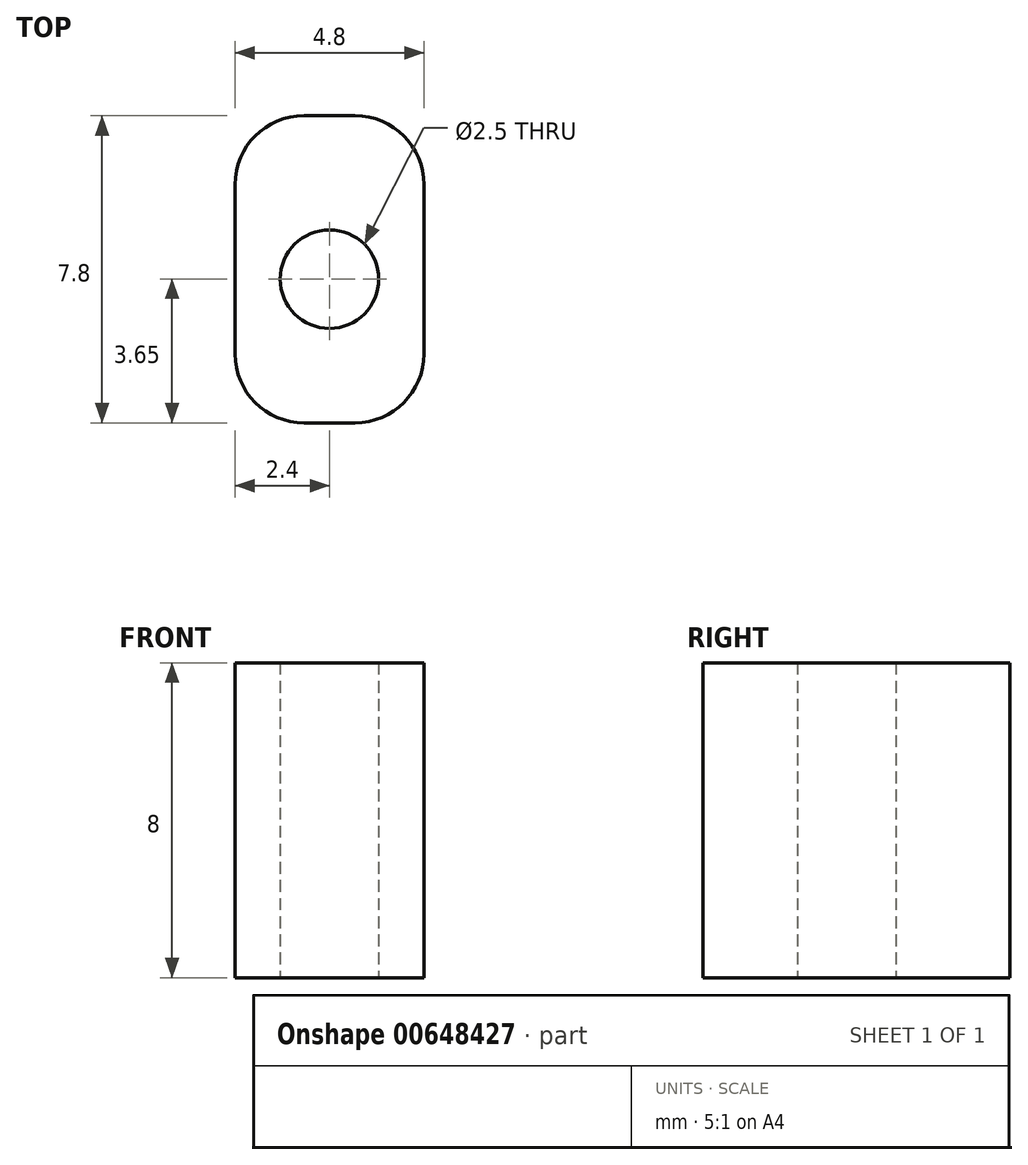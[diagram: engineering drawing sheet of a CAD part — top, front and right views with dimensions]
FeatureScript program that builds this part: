
annotation { "Feature Type Name" : "Feature", "Feature Type Description" : "" }
export const myFeature = defineFeature(function(context is Context, id is Id, definition is map)
    precondition{}
    {
        {
            var Q0;
            Q0=qCreatedBy(makeId("Top.planeOp"),FACE);
            var sketch = newSketch(context, id + "F0", { "sketchPlane" : qUnion([Q0])});
            skLineSegment(sketch, "E0.bottom", {"start": v(2.4, -3.9) * mm, "end": v(-2.4, -3.9) * mm});
            skLineSegment(sketch, "E0.top", {"start": v(2.4, 3.9) * mm, "end": v(-2.4, 3.9) * mm});
            skLineSegment(sketch, "E0.left", {"start": v(2.4, -3.9) * mm, "end": v(2.4, 3.9) * mm});
            skLineSegment(sketch, "E0.right", {"start": v(-2.4, -3.9) * mm, "end": v(-2.4, 3.9) * mm});
            skPoint(sketch, "E0.middle", {"position": v(0, 0) * mm});
            skLineSegment(sketch, "E1", {"start": v(0, 0) * mm, "end": v(0, -0.25) * mm});
            skCircle(sketch, "E2", {"center": v(0, -0.25) * mm, "radius": 1.25 * mm});
            skSolve(sketch);
        }
        {
            var Q0;
            Q0 = qSketchRegion(id + "F0", true);
            extrude(context, id + "F1", {"entities" : qUnion([Q0]), "depth" : 8 * mm, "offsetDistance" : 25 * mm});
        }
        {
            var Q0;
            Q0=makeQuery(id+"F1.opExtrude","SWEPT_EDGE",EDGE,{"disambiguationData":[OSD([sQuery(id+"F0.wireOp",EDGE,"E0.bottom"),sQuery(id+"F0.wireOp",EDGE,"E0.right")])]});
            var Q1;
            Q1=makeQuery(id+"F1.opExtrude","SWEPT_EDGE",EDGE,{"disambiguationData":[OSD([sQuery(id+"F0.wireOp",EDGE,"E0.bottom"),sQuery(id+"F0.wireOp",EDGE,"E0.left")])]});
            var Q2;
            Q2=makeQuery(id+"F1.opExtrude","SWEPT_EDGE",EDGE,{"disambiguationData":[OSD([sQuery(id+"F0.wireOp",EDGE,"E0.top"),sQuery(id+"F0.wireOp",EDGE,"E0.left")])]});
            var Q3;
            Q3=makeQuery(id+"F1.opExtrude","SWEPT_EDGE",EDGE,{"disambiguationData":[OSD([sQuery(id+"F0.wireOp",EDGE,"E0.top"),sQuery(id+"F0.wireOp",EDGE,"E0.right")])]});
            fillet(context, id + "F2", {"entities" : qUnion([Q0, Q1, Q2, Q3]), "radius" : 1.75 * mm, "tangentPropagation" : true, "allowEdgeOverflow" : false});
        }
    });
